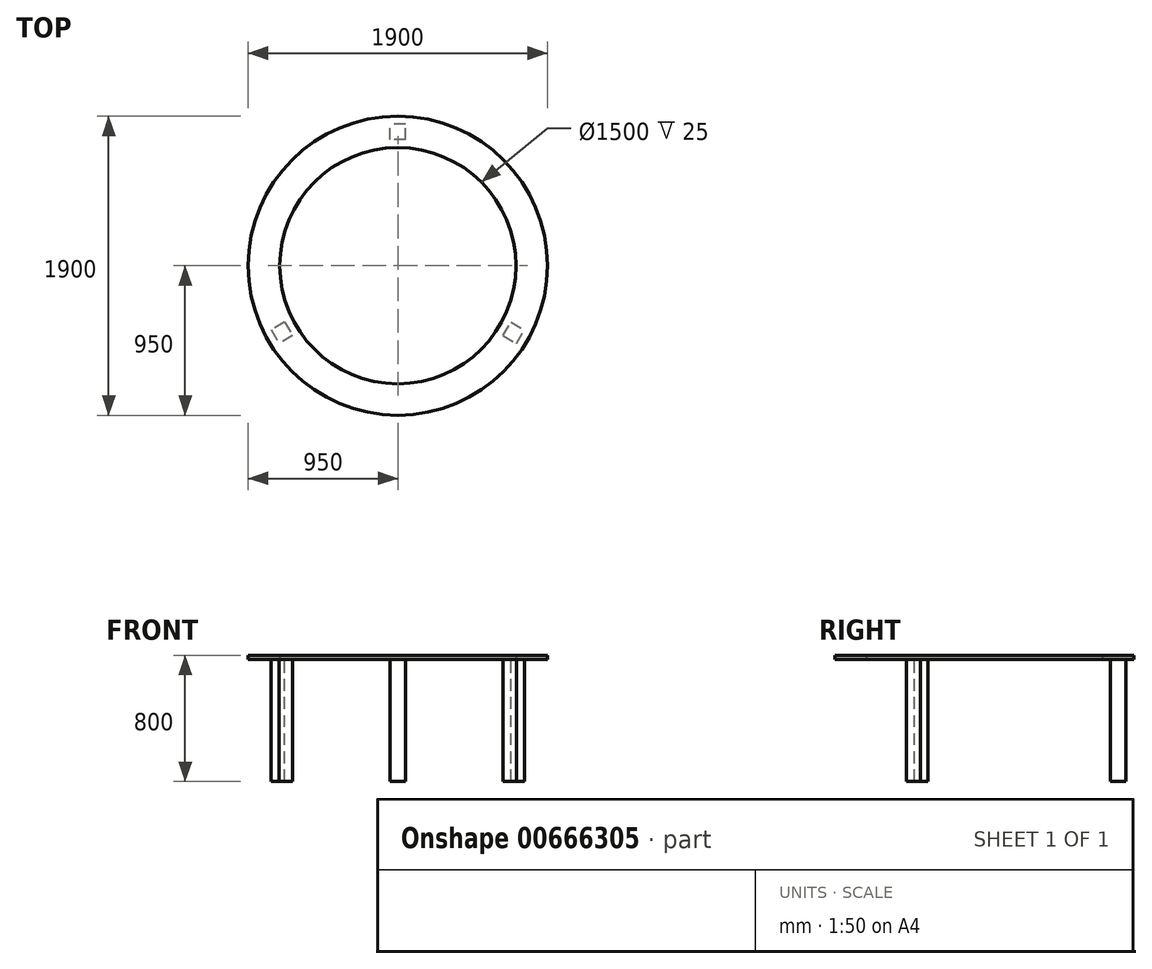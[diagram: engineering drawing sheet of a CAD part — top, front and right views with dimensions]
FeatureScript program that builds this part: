
annotation { "Feature Type Name" : "Feature", "Feature Type Description" : "" }
export const myFeature = defineFeature(function(context is Context, id is Id, definition is map)
    precondition{}
    {
        {
            var Q0;
            Q0=qCreatedBy(makeId("Top.planeOp"),FACE);
            var sketch = newSketch(context, id + "F0", { "sketchPlane" : qUnion([Q0])});
            skCircle(sketch, "E0", {"center": v(0, 0) * mm, "radius": 750 * mm});
            skCircle(sketch, "E1", {"center": v(0, 0) * mm, "radius": 950 * mm});
            skSolve(sketch);
        }
        {
            var Q0;
            Q0=qSketchRegion(id+"F0",true);
            extrude(context, id + "F1", {"entities" : qUnion([Q0]), "depth" : 25 * mm});
        }
        {
            var Q0;
            Q0=makeQuery(id+"F1.opExtrude","CAP_FACE",FACE,{"disambiguationData":[OSD([sQuery(id+"F0.wireOp",EDGE,"E0"),sQuery(id+"F0.wireOp",EDGE,"E1")])],"isStart":true});
            var sketch = newSketch(context, id + "F2", { "sketchPlane" : qUnion([Q0])});
            skLineSegment(sketch, "E2.bottom", {"start": v(50, -800) * mm, "end": v(-50, -800) * mm});
            skLineSegment(sketch, "E2.top", {"start": v(50, -900) * mm, "end": v(-50, -900) * mm});
            skLineSegment(sketch, "E2.left", {"start": v(50, -800) * mm, "end": v(50, -900) * mm});
            skLineSegment(sketch, "E2.right", {"start": v(-50, -800) * mm, "end": v(-50, -900) * mm});
            skPoint(sketch, "E2.middle", {"position": v(0, -850) * mm});
            skLineSegment(sketch, "E3", {"start": v(0, -750) * mm, "end": v(0, -950) * mm, "construction": true});
            skLineSegment(sketch, "E4.1.0", {"start": v(-649.52, 375) * mm, "end": v(-822.72, 475) * mm, "construction": true});
            skLineSegment(sketch, "E4.1.1", {"start": v(-667.82, 443.3) * mm, "end": v(-754.42, 493.3) * mm});
            skLineSegment(sketch, "E4.1.2", {"start": v(-717.82, 356.7) * mm, "end": v(-804.42, 406.7) * mm});
            skLineSegment(sketch, "E4.1.3", {"start": v(-804.42, 406.7) * mm, "end": v(-754.42, 493.3) * mm});
            skLineSegment(sketch, "E4.1.4", {"start": v(-717.82, 356.7) * mm, "end": v(-667.82, 443.3) * mm});
            skPoint(sketch, "E4.1.5", {"position": v(-736.12, 425) * mm});
            skLineSegment(sketch, "E4.2.0", {"start": v(649.52, 375) * mm, "end": v(822.72, 475) * mm, "construction": true});
            skLineSegment(sketch, "E4.2.1", {"start": v(717.82, 356.7) * mm, "end": v(804.42, 406.7) * mm});
            skLineSegment(sketch, "E4.2.2", {"start": v(667.82, 443.3) * mm, "end": v(754.42, 493.3) * mm});
            skLineSegment(sketch, "E4.2.3", {"start": v(754.42, 493.3) * mm, "end": v(804.42, 406.7) * mm});
            skLineSegment(sketch, "E4.2.4", {"start": v(667.82, 443.3) * mm, "end": v(717.82, 356.7) * mm});
            skPoint(sketch, "E4.2.5", {"position": v(736.12, 425) * mm});
            skPoint(sketch, "E4.center", {"position": v(0, 0) * mm});
            skLineSegment(sketch, "E4.anchor1", {"start": v(0, 0) * mm, "end": v(0, -950) * mm, "construction": true});
            skLineSegment(sketch, "E4.anchor2", {"start": v(0, 0) * mm, "end": v(822.72, 475) * mm, "construction": true});
            skSolve(sketch);
        }
        {
            var Q0;
            Q0=qSketchRegion(id+"F2",true);
            extrude(context, id + "F3", {"entities" : qUnion([Q0]), "operationType" : NewBodyOperationType.ADD, "depth" : 775 * mm});
        }
    });
